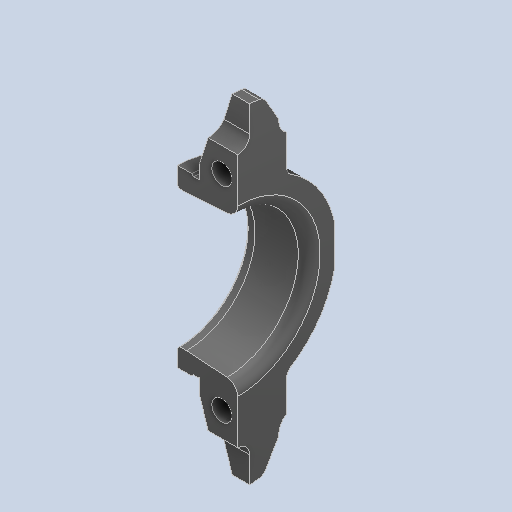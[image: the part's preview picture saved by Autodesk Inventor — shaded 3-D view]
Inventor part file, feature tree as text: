
AUTODESK INVENTOR PART (.ipt)
format: ipt  version: 2024.1 (Build 281209000, 209)  size: 161,280 bytes
history: native  units: in
note: dims shown in document units (in); Inventor stores cm internally (conversion verified against a paired STEP export)
features: chamfer x1
ambient origin geometry x8: Origin, YZ Plane, XZ Plane, XY Plane, X Axis, Y Axis, Z Axis, Center Point
bodies: Solid1 (feature_tree)
feature tree (1):
  chamfer  "Chamfer1"  [1 undecoded]
note: 1 required parameter value undecoded (feature->parameter linkage not recoverable at this tier; creation-order binding heuristic only, values carry confidence <= 0.55)
